# Revit family: Vector Vanity_BlackJack
name_source: partatom
category: Lighting Fixtures
revit_build: Autodesk Revit 2018 (Build: 20181015_0930(x64)
units: mm (PartAtom-declared; Revit-internal decimal feet)

## family parameters
Always vertical = Yes
Cut with Voids When Loaded = No
Host = Wall
Light Source = Yes
OmniClass Number = 23.80.70.00
OmniClass Title = Lighting
Part Type = Normal
Room Calculation Point = No
Round Connector Dimension = Use Diameter
Shared = No

## types (20) — shared parameters
Apparent Load = 0 VA
Color Filter = 16777215
Dimming Lamp Color Temperature Shift = <None>
Emit from Line Length = 24 "
Fax = (847) 306-3432
(847) 306-3432
Light Body = SN Satin Nickel
Light Glass = Glass Light
Manufacturer = BLACKJACK® LIGHTING
Number Of Pole = 1
Tilt Angle = 0.00°
URL = Blackjacklighting.com

## per-type parameters (varying)
| type | Light Length | Photometric Web File | Voltage |
| VEC-24V-SN-12T-27K | 24 " | VEC-24V-XX-IESNA_0122.IES | 120 V |
| VEC-24V-SN-12T-30K | 24 " | VEC-24V-XX-IESNA_0122.IES | 120 V |
| VEC-24V-SN-12T-35K | 24 " | VEC-24V-XX-IESNA_0122.IES | 120 V |
| VEC-24V-SN-12T-40K | 24 " | VEC-24V-XX-IESNA_0122.IES | 120 V |
| VEC-24V-SN-12T-50K | 24 " | VEC-24V-XX-IESNA_0122.IES | 120 V |
| VEC-24V-SN-27U-27K | 24 " | VEC-24V-XX-IESNA_0122.IES | 277 V |
| VEC-24V-SN-27U-30K | 24 " | VEC-24V-XX-IESNA_0122.IES | 277 V |
| VEC-24V-SN-27U-35K | 24 " | VEC-24V-XX-IESNA_0122.IES | 277 V |
| VEC-24V-SN-27U-40K | 24 " | VEC-24V-XX-IESNA_0122.IES | 277 V |
| VEC-24V-SN-27U-50K | 24 " | VEC-24V-XX-IESNA_0122.IES | 277 V |
| VEC-36V-SN-12T-30K | 36 " | VEC-36V-XX_IESNA_0122.IES | 120 V |
| VEC-36V-SN-12T-27K | 36 " | VEC-36V-XX_IESNA_0122.IES | 120 V |
| VEC-36V-SN-12T-35K | 36 " | VEC-36V-XX_IESNA_0122.IES | 120 V |
| VEC-36V-SN-12T-40K | 36 " | VEC-36V-XX_IESNA_0122.IES | 120 V |
| VEC-36V-SN-12T-50K | 36 " | VEC-36V-XX_IESNA_0122.IES | 120 V |
| VEC-36V-SN-27U-27K | 36 " | VEC-36V-XX_IESNA_0122.IES | 277 V |
| VEC-36V-SN-27U-30K | 36 " | VEC-36V-XX_IESNA_0122.IES | 277 V |
| VEC-36V-SN-27U-35K | 36 " | VEC-36V-XX_IESNA_0122.IES | 277 V |
| VEC-36V-SN-27U-40K | 36 " | VEC-36V-XX_IESNA_0122.IES | 277 V |
| VEC-36V-SN-27U-50K | 36 " | VEC-36V-XX_IESNA_0122.IES | 277 V |

note: column(s) folded — value = type name in every type: Model

## geometry (parser evidence)
native form markers: Sweep x3
no freeform markers — native parametric forms only
